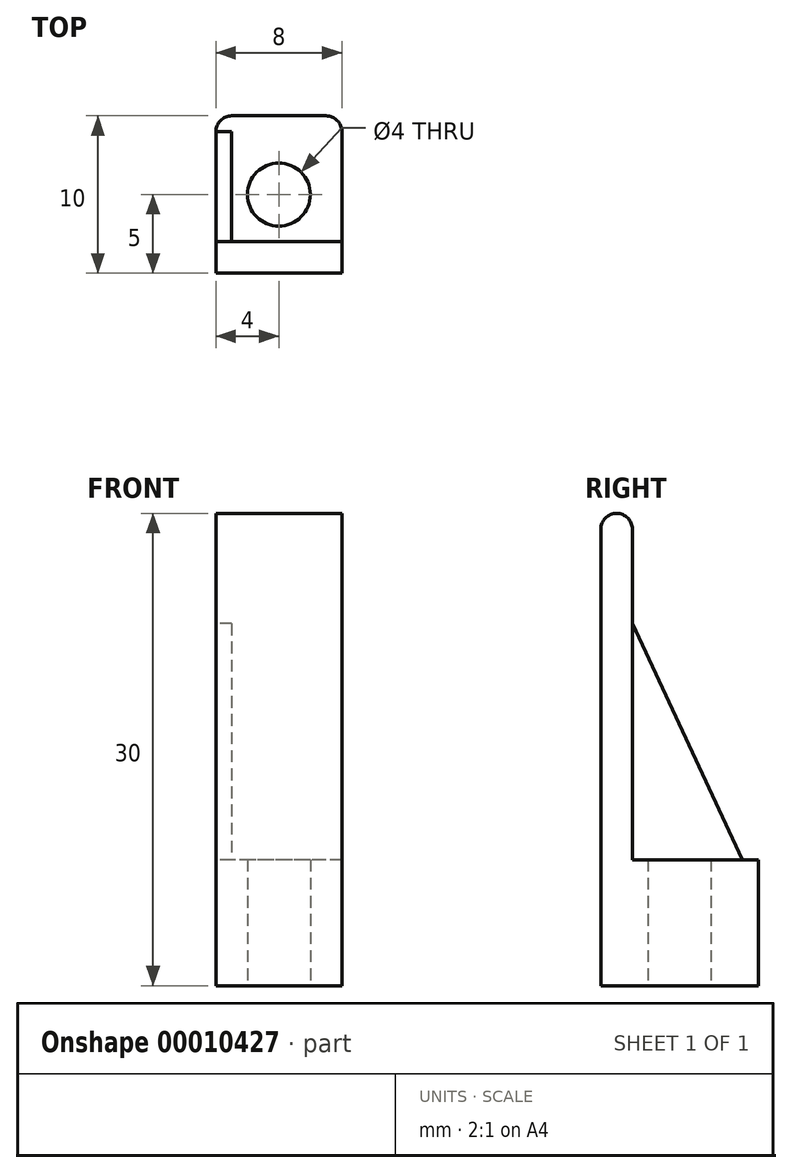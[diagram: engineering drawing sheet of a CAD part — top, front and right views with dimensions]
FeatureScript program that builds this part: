
annotation { "Feature Type Name" : "Feature", "Feature Type Description" : "" }
export const myFeature = defineFeature(function(context is Context, id is Id, definition is map)
    precondition{}
    {
        {
            var Q0;
            Q0=qCreatedBy(makeId("Top.planeOp"),FACE);
            var sketch = newSketch(context, id + "F0", { "sketchPlane" : qUnion([Q0])});
            skLineSegment(sketch, "E0.bottom", {"start": v(3, 5) * mm, "end": v(-3, 5) * mm});
            skLineSegment(sketch, "E0.top", {"start": v(4, -5) * mm, "end": v(-4, -5) * mm});
            skLineSegment(sketch, "E0.left", {"start": v(4, 4) * mm, "end": v(4, -5) * mm});
            skLineSegment(sketch, "E0.right", {"start": v(-4, 4) * mm, "end": v(-4, -5) * mm});
            skPoint(sketch, "E0.middle", {"position": v(0, 0) * mm});
            skCircle(sketch, "E1", {"center": v(0, 0) * mm, "radius": 2 * mm});
            skPoint(sketch, "E2.visualSharp", {"position": v(-4, 5) * mm});
            skArc(sketch, "E2.filletArc", {"start": v(-3, 5) * mm, "mid": v(-3.7, 4.7) * mm, "end": v(-4, 4) * mm});
            skPoint(sketch, "E3.visualSharp", {"position": v(4, 5) * mm});
            skArc(sketch, "E3.filletArc", {"start": v(4, 4) * mm, "mid": v(3.7, 4.7) * mm, "end": v(3, 5) * mm});
            skSolve(sketch);
        }
        {
            var Q0;
            Q0=makeQuery(id+"F0.imprint","IMPRINT",FACE,{"disambiguationData":[TD([[makeQuery(id+"F0.imprint","IMPRINT",EDGE,{"derivedFrom":sQuery(id+"F0.wireOp",EDGE,"E0.bottom")}),1.0]])]});
            extrude(context, id + "F1", {"entities" : qUnion([Q0]), "depth" : 8 * mm});
        }
        {
            var Q0;
            Q0=qCreatedBy(makeId("Top.planeOp"),FACE);
            var sketch = newSketch(context, id + "F2", { "sketchPlane" : qUnion([Q0])});
            skLineSegment(sketch, "E4.bottom", {"start": v(-4, -5) * mm, "end": v(4, -5) * mm});
            skLineSegment(sketch, "E4.top", {"start": v(-4, -3) * mm, "end": v(4, -3) * mm});
            skLineSegment(sketch, "E4.left", {"start": v(-4, -5) * mm, "end": v(-4, -3) * mm});
            skLineSegment(sketch, "E4.right", {"start": v(4, -5) * mm, "end": v(4, -3) * mm});
            skSolve(sketch);
        }
        {
            var Q0;
            Q0 = qSketchRegion(id + "F2", true);
            extrude(context, id + "F3", {"entities" : qUnion([Q0]), "operationType" : NewBodyOperationType.ADD, "depth" : 30 * mm});
        }
        {
            var Q0;
            Q0=makeQuery(id+"F3.opExtrude","CAP_EDGE",EDGE,{"disambiguationData":[OSD([sQuery(id+"F2.wireOp",EDGE,"E4.top")])],"isStart":false});
            var Q1;
            Q1=makeQuery(id+"F3.opExtrude","CAP_EDGE",EDGE,{"disambiguationData":[OSD([sQuery(id+"F2.wireOp",EDGE,"E4.bottom")])],"isStart":false});
            fillet(context, id + "F4", {"entities" : qUnion([Q0, Q1]), "radius" : 1 * mm, "tangentPropagation" : true, "allowEdgeOverflow" : false});
        }
        {
            var Q0;
            Q0=makeQuery(id+"F3.boolean.opBoolean","MERGE",FACE,{"derivedFrom":[makeQuery(id+"F1.opExtrude","SWEPT_FACE",FACE,{"disambiguationData":[OSD([sQuery(id+"F0.wireOp",EDGE,"E0.right")])]}),makeQuery(id+"F3.opExtrude","SWEPT_FACE",FACE,{"disambiguationData":[OSD([sQuery(id+"F2.wireOp",EDGE,"E4.left")])]})]});
            var sketch = newSketch(context, id + "F5", { "sketchPlane" : qUnion([Q0])});
            skLineSegment(sketch, "E5", {"start": v(-4, 8) * mm, "end": v(3, 23) * mm});
            skLineSegment(sketch, "E6", {"start": v(3, 23) * mm, "end": v(3, 8) * mm});
            skLineSegment(sketch, "E7", {"start": v(3, 8) * mm, "end": v(-4, 8) * mm});
            skSolve(sketch);
        }
        {
            var Q0;
            Q0 = qSketchRegion(id + "F5", true);
            extrude(context, id + "F6", {"entities" : qUnion([Q0]), "operationType" : NewBodyOperationType.ADD, "oppositeDirection" : true, "depth" : 1 * mm});
        }
    });
